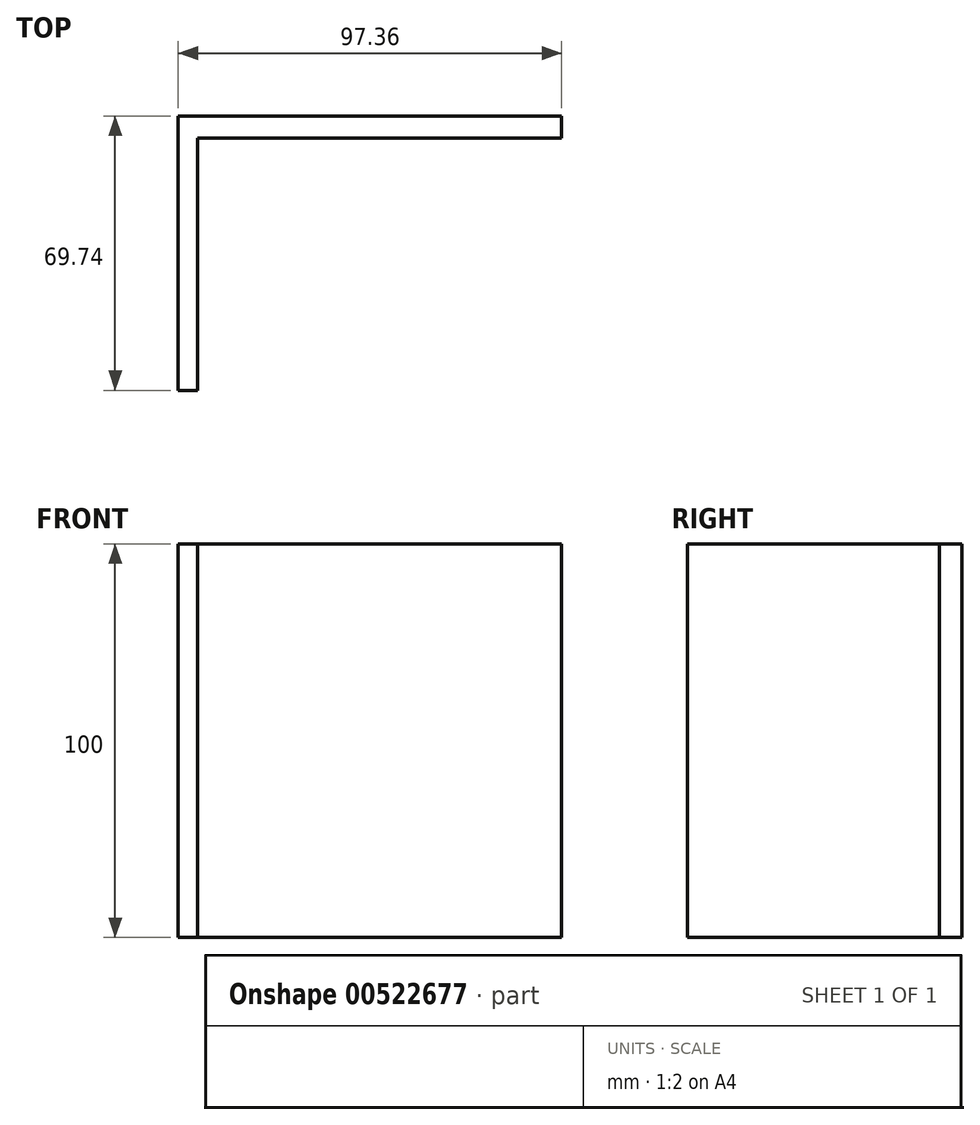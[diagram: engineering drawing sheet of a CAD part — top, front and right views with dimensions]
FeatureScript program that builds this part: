
annotation { "Feature Type Name" : "Feature", "Feature Type Description" : "" }
export const myFeature = defineFeature(function(context is Context, id is Id, definition is map)
    precondition{}
    {
        {
            var Q0;
            Q0=qCreatedBy(makeId("Top.planeOp"),FACE);
            var sketch = newSketch(context, id + "F0", { "sketchPlane" : qUnion([Q0])});
            skLineSegment(sketch, "E0.bottom", {"start": v(-48.48, 2.55) * mm, "end": v(-43.59, 2.55) * mm});
            skLineSegment(sketch, "E0.top", {"start": v(-48.48, 66.6) * mm, "end": v(-43.59, 66.6) * mm});
            skLineSegment(sketch, "E0.left", {"start": v(-48.48, 2.55) * mm, "end": v(-48.48, 66.6) * mm});
            skLineSegment(sketch, "E0.right", {"start": v(-43.59, 2.55) * mm, "end": v(-43.59, 66.6) * mm});
            skLineSegment(sketch, "E1.bottom", {"start": v(-48.48, 66.6) * mm, "end": v(48.88, 66.6) * mm});
            skLineSegment(sketch, "E1.top", {"start": v(-48.48, 72.29) * mm, "end": v(48.88, 72.29) * mm});
            skLineSegment(sketch, "E1.left", {"start": v(-48.48, 66.6) * mm, "end": v(-48.48, 72.29) * mm});
            skLineSegment(sketch, "E1.right", {"start": v(48.88, 66.6) * mm, "end": v(48.88, 72.29) * mm});
            skLineSegment(sketch, "E2.bottom", {"start": v(48.88, 72.29) * mm, "end": v(48.88, 72.29) * mm});
            skLineSegment(sketch, "E2.top", {"start": v(48.88, 66.6) * mm, "end": v(48.88, 66.6) * mm});
            skLineSegment(sketch, "E2.left", {"start": v(48.88, 72.29) * mm, "end": v(48.88, 66.6) * mm});
            skLineSegment(sketch, "E2.right", {"start": v(48.88, 72.29) * mm, "end": v(48.88, 66.6) * mm});
            skLineSegment(sketch, "E3.bottom", {"start": v(48.88, 66.6) * mm, "end": v(43.59, 66.6) * mm});
            skLineSegment(sketch, "E3.top", {"start": v(48.88, 0) * mm, "end": v(43.59, 0) * mm});
            skLineSegment(sketch, "E3.left", {"start": v(48.88, 66.6) * mm, "end": v(48.88, 0) * mm});
            skLineSegment(sketch, "E3.right", {"start": v(43.59, 66.6) * mm, "end": v(43.59, 0) * mm});
            skSolve(sketch);
        }
        {
            var Q0;
            Q0=makeQuery(id+"F0.imprint","IMPRINT",FACE,{"disambiguationData":[TD([[makeQuery(id+"F0.imprint","IMPRINT",EDGE,{"derivedFrom":sQuery(id+"F0.wireOp",EDGE,"E1.top")}),-1.0]])]});
            var Q1;
            Q1=makeQuery(id+"F0.imprint","IMPRINT",FACE,{"disambiguationData":[TD([[makeQuery(id+"F0.imprint","IMPRINT",EDGE,{"derivedFrom":sQuery(id+"F0.wireOp",EDGE,"E0.bottom")}),1.0]])]});
            var Q2;
            Q2=makeQuery(id+"F0.imprint","IMPRINT",FACE,{"disambiguationData":[TD([[makeQuery(id+"F0.imprint","IMPRINT",EDGE,{"derivedFrom":sQuery(id+"F0.wireOp",EDGE,"E3.bottom")}),1.0]])]});
            extrude(context, id + "F1", {"entities" : qUnion([Q0, Q1, Q2]), "depth" : 100 * mm, "offsetDistance" : 25 * mm});
        }
    });
